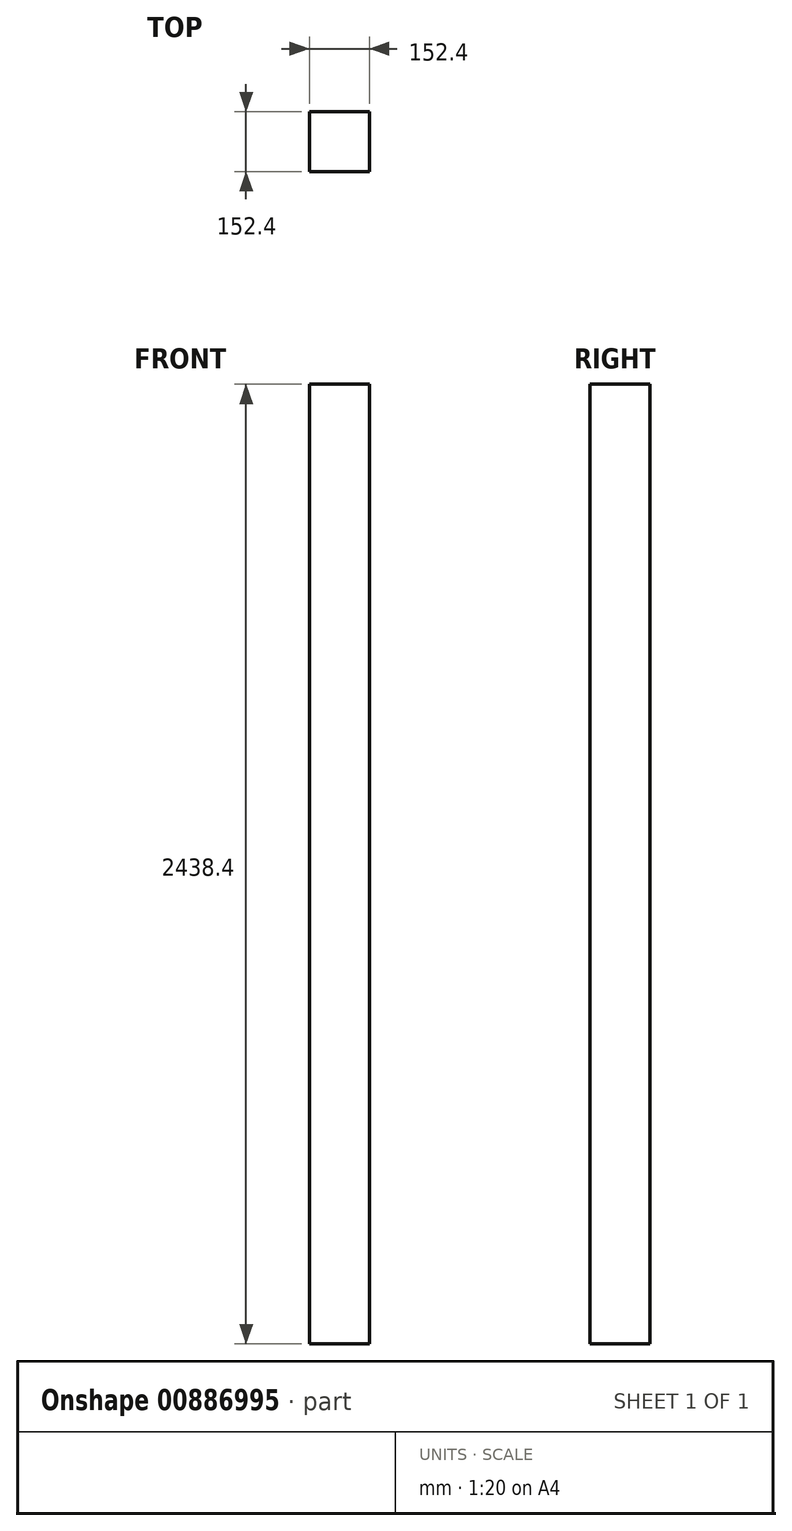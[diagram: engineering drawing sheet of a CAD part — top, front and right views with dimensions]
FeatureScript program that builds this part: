
annotation { "Feature Type Name" : "Feature", "Feature Type Description" : "" }
export const myFeature = defineFeature(function(context is Context, id is Id, definition is map)
    precondition{}
    {
        {
            var Q0;
            Q0=qCreatedBy(makeId("Top.planeOp"),FACE);
            var sketch = newSketch(context, id + "F0", { "sketchPlane" : qUnion([Q0])});
            skLineSegment(sketch, "E0.bottom", {"start": v(0, 0) * mm, "end": v(152.4, 0) * mm});
            skLineSegment(sketch, "E0.top", {"start": v(0, 152.4) * mm, "end": v(152.4, 152.4) * mm});
            skLineSegment(sketch, "E0.left", {"start": v(0, 0) * mm, "end": v(0, 152.4) * mm});
            skLineSegment(sketch, "E0.right", {"start": v(152.4, 0) * mm, "end": v(152.4, 152.4) * mm});
            skSolve(sketch);
        }
        {
            var Q0;
            Q0 = qSketchRegion(id + "F0", true);
            extrude(context, id + "F1", {"entities" : qUnion([Q0]), "depth" : 2438.4 * mm, "offsetDistance" : 25.4 * mm});
        }
    });
